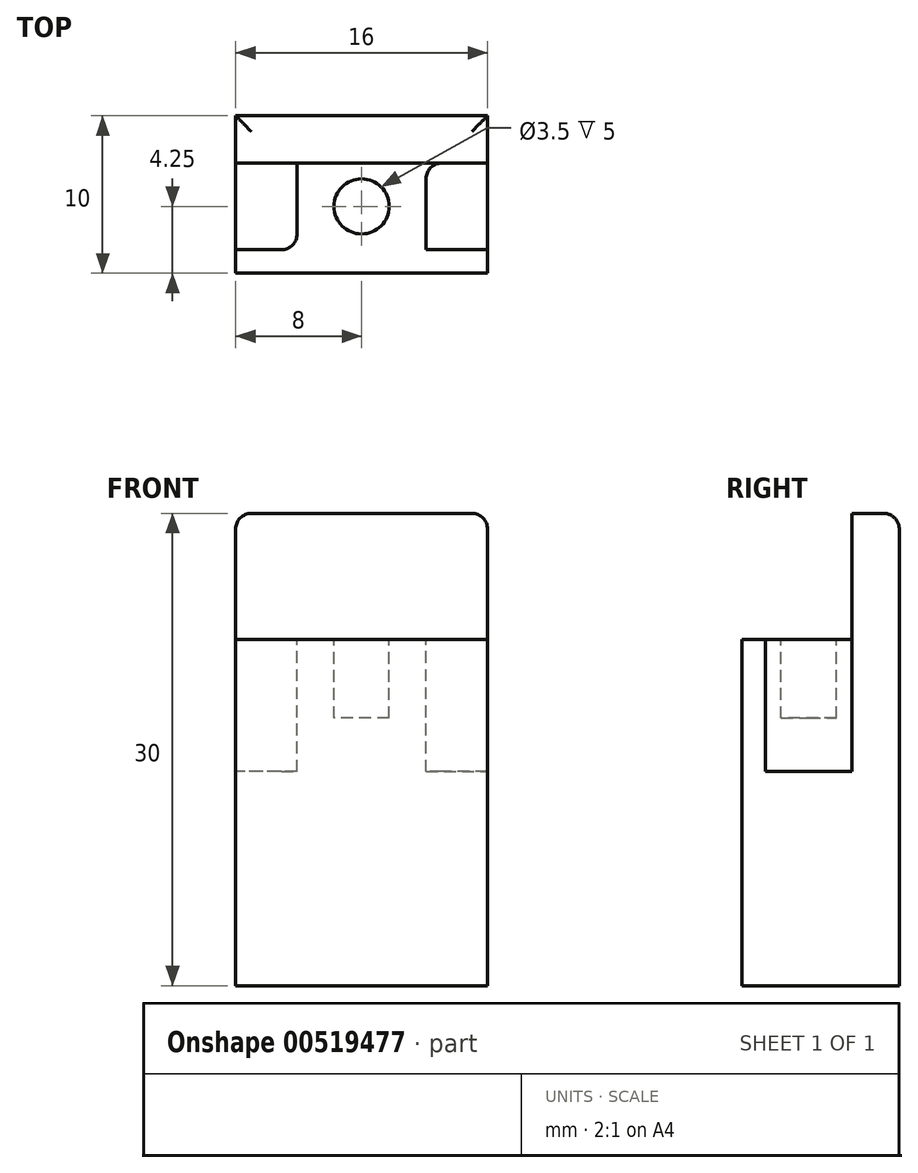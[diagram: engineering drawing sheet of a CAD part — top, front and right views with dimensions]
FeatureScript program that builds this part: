
annotation { "Feature Type Name" : "Feature", "Feature Type Description" : "" }
export const myFeature = defineFeature(function(context is Context, id is Id, definition is map)
    precondition{}
    {
        {
            var Q0;
            Q0=qCreatedBy(makeId("Top.planeOp"),FACE);
            var sketch = newSketch(context, id + "F0", { "sketchPlane" : qUnion([Q0])});
            skLineSegment(sketch, "E0.bottom", {"start": v(-8, -5) * mm, "end": v(8, -5) * mm});
            skLineSegment(sketch, "E0.top", {"start": v(-8, 5) * mm, "end": v(8, 5) * mm});
            skLineSegment(sketch, "E0.left", {"start": v(-8, -5) * mm, "end": v(-8, 5) * mm});
            skLineSegment(sketch, "E0.right", {"start": v(8, -5) * mm, "end": v(8, 5) * mm});
            skSolve(sketch);
        }
        {
            var Q0;
            Q0 = qSketchRegion(id + "F0", true);
            extrude(context, id + "F1", {"entities" : qUnion([Q0]), "depth" : 30 * mm, "offsetDistance" : 25 * mm});
        }
        {
            var Q0;
            Q0=makeQuery(id+"F1.opExtrude","CAP_FACE",FACE,{"disambiguationData":[OSD([sQuery(id+"F0.wireOp",EDGE,"E0.bottom"),sQuery(id+"F0.wireOp",EDGE,"E0.top"),sQuery(id+"F0.wireOp",EDGE,"E0.left"),sQuery(id+"F0.wireOp",EDGE,"E0.right")])],"isStart":false});
            var sketch = newSketch(context, id + "F2", { "sketchPlane" : qUnion([Q0])});
            skLineSegment(sketch, "E1", {"start": v(-8, -5) * mm, "end": v(8, -5) * mm});
            skLineSegment(sketch, "E2", {"start": v(8, -5) * mm, "end": v(8, 2) * mm});
            skLineSegment(sketch, "E3", {"start": v(8, 2) * mm, "end": v(-8, 2) * mm});
            skLineSegment(sketch, "E4", {"start": v(-8, 2) * mm, "end": v(-8, -5) * mm});
            skSolve(sketch);
        }
        {
            var Q0;
            Q0 = qSketchRegion(id + "F2", true);
            extrude(context, id + "F3", {"entities" : qUnion([Q0]), "operationType" : NewBodyOperationType.REMOVE, "oppositeDirection" : true, "depth" : 8 * mm, "offsetDistance" : 25 * mm});
        }
        {
            var Q0;
            Q0=makeQuery(id+"F3.boolean.opBoolean","COPY",FACE,{"derivedFrom":makeQuery(id+"F3.opExtrude","CAP_FACE",FACE,{"disambiguationData":[OSD([sQuery(id+"F2.wireOp",EDGE,"E1"),sQuery(id+"F2.wireOp",EDGE,"E2"),sQuery(id+"F2.wireOp",EDGE,"E3"),sQuery(id+"F2.wireOp",EDGE,"E4")])],"isStart":false})});
            var sketch = newSketch(context, id + "F4", { "sketchPlane" : qUnion([Q0])});
            skLineSegment(sketch, "E5", {"start": v(0, 5.69) * mm, "end": v(0, -9.43) * mm, "construction": true});
            skLineSegment(sketch, "E6", {"start": v(-8, 2) * mm, "end": v(-4.1, 2) * mm});
            skLineSegment(sketch, "E7", {"start": v(-4.1, 2) * mm, "end": v(-4.1, -3.5) * mm});
            skLineSegment(sketch, "E8", {"start": v(-4.1, -3.5) * mm, "end": v(-8, -3.5) * mm});
            skLineSegment(sketch, "E9", {"start": v(-8, -3.5) * mm, "end": v(-8, 2) * mm});
            skLineSegment(sketch, "E10.MirrorCS", {"start": v(8, 2) * mm, "end": v(4.1, 2) * mm});
            skLineSegment(sketch, "E11.MirrorCS", {"start": v(8, -3.5) * mm, "end": v(8, 2) * mm});
            skLineSegment(sketch, "E12.MirrorCS", {"start": v(4.1, -3.5) * mm, "end": v(8, -3.5) * mm});
            skLineSegment(sketch, "E13.MirrorCS", {"start": v(4.1, 2) * mm, "end": v(4.1, -3.5) * mm});
            skSolve(sketch);
        }
        {
            var Q0;
            Q0 = qSketchRegion(id + "F4", true);
            var Q1;
            Q1=makeQuery(id+"F4.imprint","IMPRINT",FACE,{"disambiguationData":[TD([[makeQuery(id+"F4.imprint","IMPRINT",EDGE,{"derivedFrom":sQuery(id+"F4.wireOp",EDGE,"RNKxOxFS-nhTW-4vel-XwOF-Vy1jTYFh1dKW")}),-1.0]])]});
            extrude(context, id + "F5", {"entities" : qUnion([Q0, Q1]), "operationType" : NewBodyOperationType.REMOVE, "oppositeDirection" : true, "depth" : 8.4 * mm, "offsetDistance" : 25 * mm});
        }
        {
            var Q0;
            Q0=makeQuery(id+"F3.boolean.opBoolean","COPY",FACE,{"derivedFrom":makeQuery(id+"F3.opExtrude","CAP_FACE",FACE,{"disambiguationData":[OSD([sQuery(id+"F2.wireOp",EDGE,"E1"),sQuery(id+"F2.wireOp",EDGE,"E2"),sQuery(id+"F2.wireOp",EDGE,"E3"),sQuery(id+"F2.wireOp",EDGE,"E4")])],"isStart":false})});
            var sketch = newSketch(context, id + "F6", { "sketchPlane" : qUnion([Q0])});
            skCircle(sketch, "E14", {"center": v(0, -0.75) * mm, "radius": 1.75 * mm});
            skSolve(sketch);
        }
        {
            var Q0;
            Q0=makeQuery(id+"F6.imprint","IMPRINT",FACE,{"disambiguationData":[TD([[makeQuery(id+"F6.imprint","IMPRINT",EDGE,{"derivedFrom":sQuery(id+"F6.wireOp",EDGE,"E14")}),1.0]])]});
            extrude(context, id + "F7", {"entities" : qUnion([Q0]), "operationType" : NewBodyOperationType.REMOVE, "oppositeDirection" : true, "depth" : 5 * mm, "offsetDistance" : 25 * mm});
        }
        {
            var Q0;
            Q0=makeQuery(id+"F5.boolean.opBoolean","COPY",EDGE,{"derivedFrom":makeQuery(id+"F5.opExtrude","SWEPT_EDGE",EDGE,{"disambiguationData":[OSD([sQuery(id+"F2.wireOp",EDGE,"E3"),sQuery(id+"F4.wireOp",EDGE,"E10.MirrorCS"),sQuery(id+"F4.wireOp",EDGE,"E13.MirrorCS")])]})});
            var Q1;
            Q1=makeQuery(id+"F5.boolean.opBoolean","COPY",EDGE,{"derivedFrom":makeQuery(id+"F5.opExtrude","CAP_EDGE",EDGE,{"disambiguationData":[OSD([sQuery(id+"F4.wireOp",EDGE,"E13.MirrorCS")])],"isStart":true})});
            var Q2;
            Q2=makeQuery(id+"F5.boolean.opBoolean","COPY",EDGE,{"derivedFrom":makeQuery(id+"F5.opExtrude","CAP_EDGE",EDGE,{"disambiguationData":[OSD([sQuery(id+"F4.wireOp",EDGE,"E7")])],"isStart":true})});
            var Q3;
            Q3=makeQuery(id+"F5.boolean.opBoolean","COPY",EDGE,{"derivedFrom":makeQuery(id+"F5.opExtrude","SWEPT_EDGE",EDGE,{"disambiguationData":[OSD([sQuery(id+"F4.wireOp",EDGE,"E7"),sQuery(id+"F4.wireOp",EDGE,"E8")])]})});
            var Q4;
            Q4=makeQuery(id+"F5.boolean.opBoolean","COPY",EDGE,{"derivedFrom":makeQuery(id+"F5.opExtrude","CAP_EDGE",EDGE,{"disambiguationData":[OSD([sQuery(id+"F4.wireOp",EDGE,"E12.MirrorCS")])],"isStart":true})});
            var Q5;
            Q5=makeQuery(id+"F1.opExtrude","CAP_EDGE",EDGE,{"disambiguationData":[OSD([sQuery(id+"F0.wireOp",EDGE,"E0.right")])],"isStart":false});
            var Q6;
            Q6=makeQuery(id+"F1.opExtrude","CAP_EDGE",EDGE,{"disambiguationData":[OSD([sQuery(id+"F0.wireOp",EDGE,"E0.left")])],"isStart":false});
            var Q7;
            Q7=makeQuery(id+"F3.boolean.opBoolean","COPY",EDGE,{"derivedFrom":makeQuery(id+"F3.opExtrude","CAP_EDGE",EDGE,{"disambiguationData":[OSD([sQuery(id+"F2.wireOp",EDGE,"E3")])],"isStart":true})});
            var Q8;
            Q8=makeQuery(id+"F1.opExtrude","CAP_EDGE",EDGE,{"disambiguationData":[OSD([sQuery(id+"F0.wireOp",EDGE,"E0.top")])],"isStart":false});
            var Q9;
            Q9=makeQuery(id+"F5.boolean.opBoolean","MERGE",EDGE,{"derivedFrom":[makeQuery(id+"F3.boolean.opBoolean","COPY",EDGE,{"derivedFrom":makeQuery(id+"F3.opExtrude","SWEPT_EDGE",EDGE,{"disambiguationData":[OSD([sQuery(id+"F0.wireOp",EDGE,"E0.left"),sQuery(id+"F2.wireOp",EDGE,"E3"),sQuery(id+"F2.wireOp",EDGE,"E4")])]})}),makeQuery(id+"F5.opExtrude","SWEPT_EDGE",EDGE,{"disambiguationData":[OSD([sQuery(id+"F4.wireOp",EDGE,"E6"),sQuery(id+"F4.wireOp",EDGE,"E9")])]})]});
            var Q10;
            Q10=makeQuery(id+"F5.boolean.opBoolean","MERGE",EDGE,{"derivedFrom":[makeQuery(id+"F3.boolean.opBoolean","COPY",EDGE,{"derivedFrom":makeQuery(id+"F3.opExtrude","SWEPT_EDGE",EDGE,{"disambiguationData":[OSD([sQuery(id+"F0.wireOp",EDGE,"E0.right"),sQuery(id+"F2.wireOp",EDGE,"E2"),sQuery(id+"F2.wireOp",EDGE,"E3")])]})}),makeQuery(id+"F5.opExtrude","SWEPT_EDGE",EDGE,{"disambiguationData":[OSD([sQuery(id+"F4.wireOp",EDGE,"E10.MirrorCS"),sQuery(id+"F4.wireOp",EDGE,"E11.MirrorCS")])]})]});
            fillet(context, id + "F8", {"entities" : qUnion([Q0, Q1, Q2, Q3, Q4, Q5, Q6, Q7, Q8, Q9, Q10]), "radius" : 1 * mm, "tangentPropagation" : true, "allowEdgeOverflow" : false});
        }
    });
